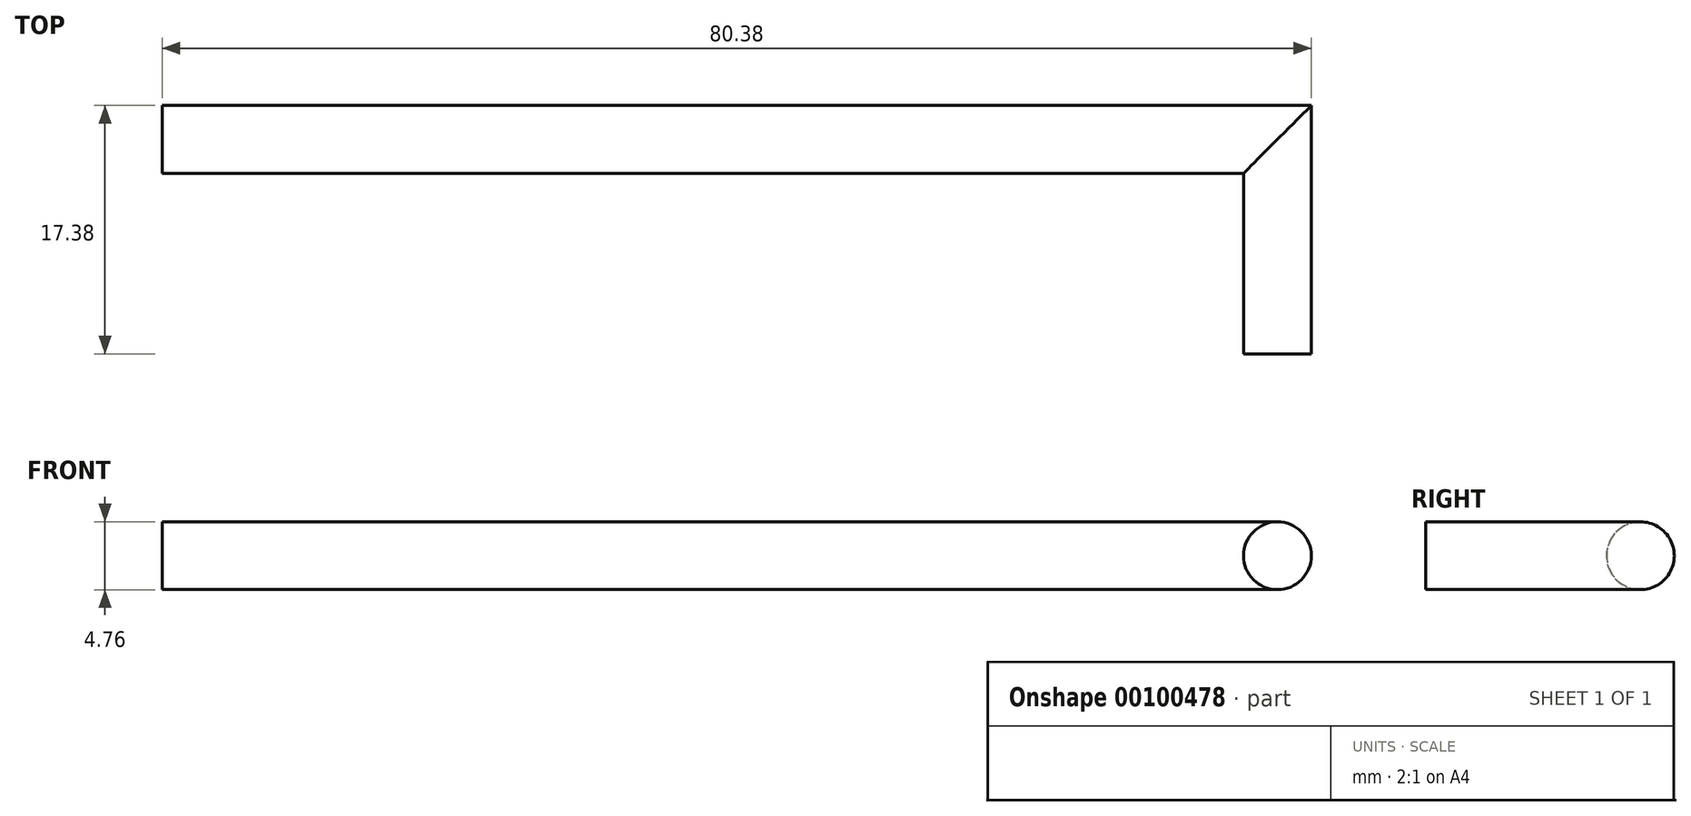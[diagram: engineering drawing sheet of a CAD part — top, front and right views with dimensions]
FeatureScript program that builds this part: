
annotation { "Feature Type Name" : "Feature", "Feature Type Description" : "" }
export const myFeature = defineFeature(function(context is Context, id is Id, definition is map)
    precondition{}
    {
        {
            var Q0;
            Q0=qCreatedBy(makeId("Front.planeOp"),FACE);
            var sketch = newSketch(context, id + "F0", { "sketchPlane" : qUnion([Q0])});
            skLineSegment(sketch, "E0", {"start": v(-39, 0) * mm, "end": v(39, 0) * mm});
            skSolve(sketch);
        }
        {
            var Q0;
            Q0=qCreatedBy(makeId("Right.planeOp"),FACE);
            var Q1;
            Q1=sQuery(id+"F0.wireOp",VERTEX,"E0.start");
            cPlane(context, id + "F1", {"entities" : qUnion([Q0, Q1]), "cplaneType" : CPlaneType.PLANE_POINT, "offset" : 25 * mm, "width" : 150 * mm, "height" : 150 * mm});
        }
        {
            var Q0;
            Q0=qCreatedBy(id+"F1.planeOp",FACE);
            var sketch = newSketch(context, id + "F2", { "sketchPlane" : qUnion([Q0])});
            skCircle(sketch, "E1", {"center": v(0, 0) * mm, "radius": 2.38 * mm});
            skSolve(sketch);
        }
        {
            var Q0;
            Q0=sQuery(id+"F0.wireOp",VERTEX,"E0.end");
            var Q1;
            Q1=qCreatedBy(makeId("Right.planeOp"),FACE);
            cPlane(context, id + "F3", {"entities" : qUnion([Q0, Q1]), "cplaneType" : CPlaneType.PLANE_POINT, "offset" : 25 * mm, "width" : 150 * mm, "height" : 150 * mm});
        }
        {
            var Q0;
            Q0=qCreatedBy(id+"F3.planeOp",FACE);
            var sketch = newSketch(context, id + "F4", { "sketchPlane" : qUnion([Q0])});
            skLineSegment(sketch, "E2", {"start": v(0, 0) * mm, "end": v(-15, 0) * mm});
            skSolve(sketch);
        }
        {
            var Q0;
            Q0=makeQuery(id+"F2.imprint","IMPRINT",FACE,{"disambiguationData":[TD([[makeQuery(id+"F2.imprint","IMPRINT",EDGE,{"derivedFrom":sQuery(id+"F2.wireOp",EDGE,"E1")}),1.0]])]});
            var Q1;
            Q1=sQuery(id+"F0.wireOp",EDGE,"E0");
            var Q2;
            Q2=sQuery(id+"F4.wireOp",EDGE,"E2");
            sweep(context, id + "F5", {"profiles" : qUnion([Q0]), "path" : qUnion([Q1, Q2])});
        }
    });
